# Revit family: AVON SIDE FIX
name_source: partatom
category: Generic Models
units: mm (PartAtom-declared; Revit-internal decimal feet)

## family parameters
Always vertical = No
Can host rebar = No
Cut with Voids When Loaded = No
Part Type = Normal
Room Calculation Point = No
Round Connector Dimension = Use Diameter
Shared = No
Work Plane-Based = No

## types (5) — shared parameters
Manufacturer = UNEX SYSTEMS
Max Post Spacing = 1000 mm  [stored 3.28084 ft]
Top Rail Height = 24 mm  [stored 0.0787402 ft]
URL = WWW.UNEX.CO.NZ
zero-valued in all types: Default Elevation

## per-type parameters (varying)
| type | ART TOP RAIL | Description | HEIGHT | Keynote | LENGTH | Model | PPR TOP RAIL | Pannel QTY | Post Height | Post QTY | UNDER SPACE | VRE TOP RAIL | VRR TOP RAIL | VRT TOP RAIL |
| AVON WITH VRE (SIDE FIX) | No | UNEX AVON FRAMED GLASS WITH VRE TOP RAIL | 1150 mm  [stored 3.77297 ft] | UNEX SYSTEMS, AVON SIDE FIX BALUSTRADE | 2450 mm  [stored 8.03806 ft] | UNEX, AVON SIDE FIX (VRE) | No | 2 | 1126 mm  [stored 3.69423 ft] | 3 | 260 mm  [stored 0.853018 ft] | Yes | No | No |
| AVON WITH PRR (SIDE FIX) | No | UNEX SYSTEMS, AVON SIDE FIX BALUSTRADE | 1542 mm | UNEX, AVON SIDE FIX (PRR) | 2540 mm | UNEX AVON FRAMED GLASS WITH PRR TOP RAIL | Yes | 3 | 1518 mm | 4 | 250 mm  [stored 0.82021 ft] | No | No | No |
| AVON WITH ART (SIDE FIX) | Yes | UNEX AVON FRAMED GLASS WITH ART TOP RAIL | 1478 mm | UNEX SYSTEMS, AVON SIDE FIX BALUSTRADE | 2685 mm | UNEX, AVON SIDE FIX (ART) | No | 3 | 1454 mm | 4 | 300 mm | No | No | No |
| AVON WITH VRT (SIDE FIX) | No | UNEX AVON FRAMED GLASS WITH VRT TOP RAIL | 1478 mm | UNEX SYSTEMS, AVON SIDE FIX BALUSTRADE | 2345 mm | UNEX, AVON SIDE FIX (VRT) | No | 2 | 1454 mm | 3 | 264 mm | No | No | Yes |
| AVON WITH VRR (SIDE FIX) | No | UNEX AVON FRAMED GLASS WITH VRR TOP RAIL | 1150 mm  [stored 3.77297 ft] | UNEX SYSTEMS, AVON SIDE FIX BALUSTRADE | 2800 mm | UNEX AVON WITH VRR TOP RAIL | No | 3 | 1126 mm  [stored 3.69423 ft] | 4 | 350 mm  [stored 1.14829 ft] | No | Yes | No |

note: [stored X ft] marks values corroborated as IEEE doubles in the binary element streams (Revit-internal decimal feet)

## geometry (parser evidence)
native form markers: Sweep x25
no freeform markers — native parametric forms only
